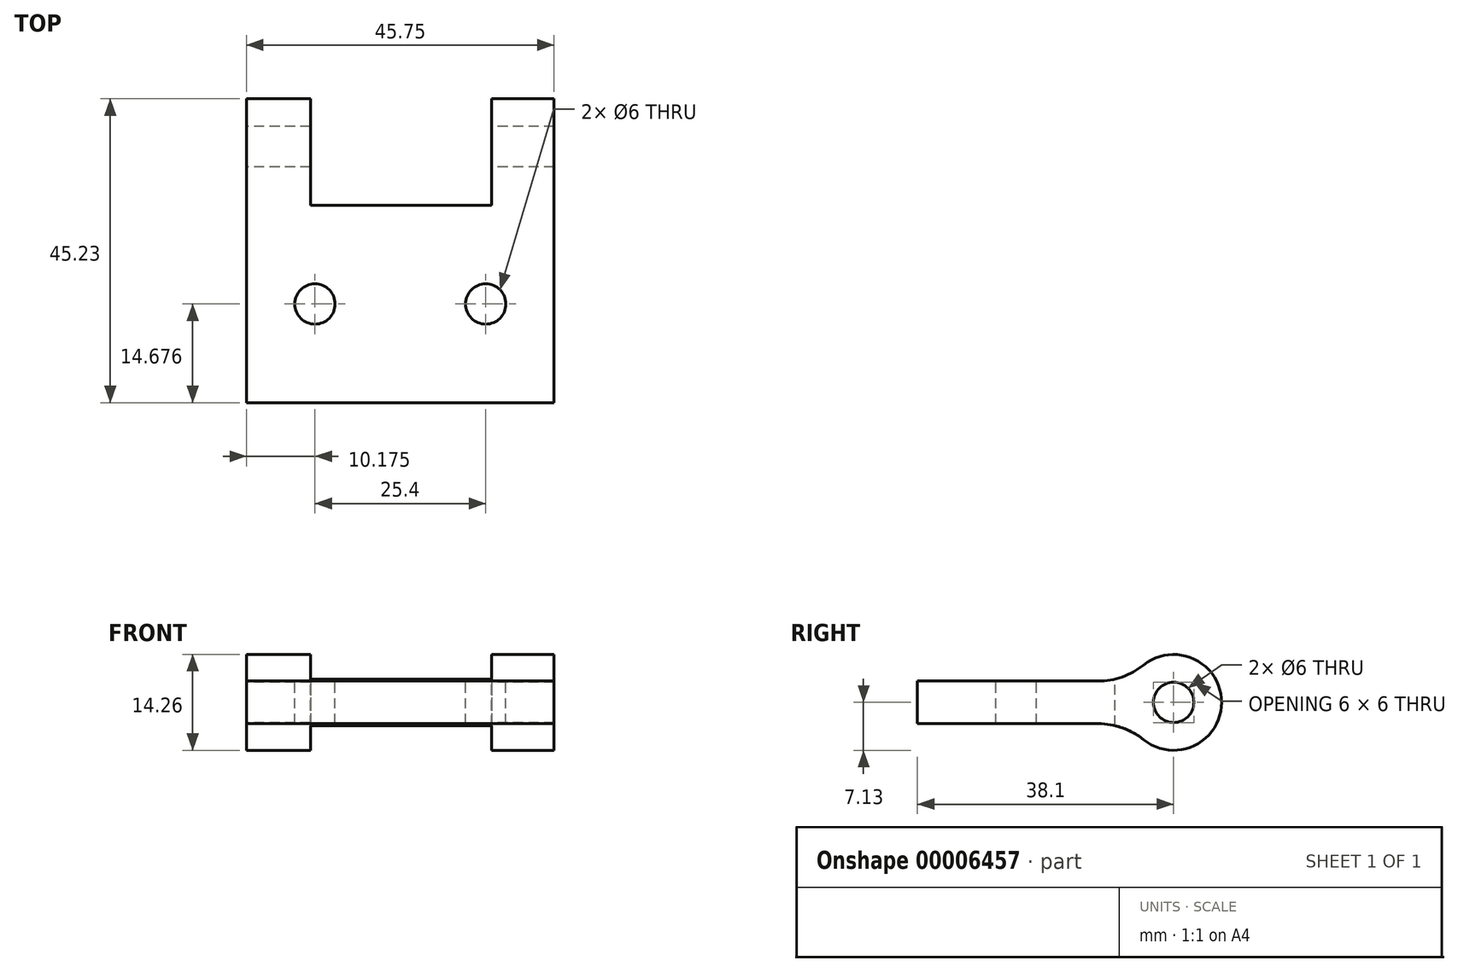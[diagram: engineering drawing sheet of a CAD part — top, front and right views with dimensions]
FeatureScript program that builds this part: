
annotation { "Feature Type Name" : "Feature", "Feature Type Description" : "" }
export const myFeature = defineFeature(function(context is Context, id is Id, definition is map)
    precondition{}
    {
        {
            var Q0;
            Q0=qCreatedBy(makeId("Right.planeOp"),FACE);
            var sketch = newSketch(context, id + "F0", { "sketchPlane" : qUnion([Q0])});
            skCircle(sketch, "E0", {"center": v(0, 0) * mm, "radius": 3 * mm});
            skArc(sketch, "E1", {"start": v(-6.38, -3.17) * mm, "mid": v(7.13, 0) * mm, "end": v(-6.38, 3.17) * mm});
            skLineSegment(sketch, "E2.bottom", {"start": v(-6.38, 3.17) * mm, "end": v(-38.1, 3.18) * mm});
            skLineSegment(sketch, "E2.top", {"start": v(-6.38, -3.17) * mm, "end": v(-38.1, -3.18) * mm});
            skLineSegment(sketch, "E2.right", {"start": v(-38.1, 3.18) * mm, "end": v(-38.1, -3.18) * mm});
            skSolve(sketch);
        }
        {
            var Q0;
            Q0 = qSketchRegion(id + "F0", true);
            extrude(context, id + "F1", {"entities" : qUnion([Q0]), "depth" : 45.75 * mm});
        }
        {
            var Q0;
            Q0=qCreatedBy(makeId("Top.planeOp"),FACE);
            var sketch = newSketch(context, id + "F2", { "sketchPlane" : qUnion([Q0])});
            skLineSegment(sketch, "E3.bottom", {"start": v(9.52, 7.13) * mm, "end": v(36.48, 7.13) * mm});
            skLineSegment(sketch, "E3.top", {"start": v(9.53, -8.75) * mm, "end": v(36.48, -8.75) * mm});
            skLineSegment(sketch, "E3.left", {"start": v(9.52, 7.13) * mm, "end": v(9.53, -8.75) * mm});
            skLineSegment(sketch, "E3.right", {"start": v(36.48, 7.13) * mm, "end": v(36.48, -8.75) * mm});
            skSolve(sketch);
        }
        {
            var Q0;
            Q0 = qSketchRegion(id + "F2", true);
            extrude(context, id + "F3", {"entities" : qUnion([Q0]), "operationType" : NewBodyOperationType.REMOVE, "endBound" : BoundingType.THROUGH_ALL, "oppositeDirection" : true, "depth" : 25.4 * mm, "hasSecondDirection" : true, "secondDirectionBound" : SecondDirectionBoundingType.THROUGH_ALL, "secondDirectionOppositeDirection" : false, "secondDirectionDepth" : 25.4 * mm});
        }
        {
            var Q0;
            Q0=makeQuery(id+"F1.opExtrude","SWEPT_FACE",FACE,{"disambiguationData":[OSD([sQuery(id+"F0.wireOp",EDGE,"E2.bottom")])]});
            var sketch = newSketch(context, id + "F4", { "sketchPlane" : qUnion([Q0])});
            skCircle(sketch, "E4", {"center": v(10.18, -23.42) * mm, "radius": 3 * mm});
            skCircle(sketch, "E5", {"center": v(35.58, -23.42) * mm, "radius": 3 * mm});
            skLineSegment(sketch, "E6", {"start": v(10.18, -23.42) * mm, "end": v(0, -23.42) * mm, "construction": true});
            skLineSegment(sketch, "E7", {"start": v(35.58, -23.42) * mm, "end": v(45.75, -23.42) * mm, "construction": true});
            skLineSegment(sketch, "E8", {"start": v(10.18, -23.42) * mm, "end": v(10.18, -8.75) * mm, "construction": true});
            skLineSegment(sketch, "E9", {"start": v(10.18, -23.42) * mm, "end": v(10.18, -38.1) * mm, "construction": true});
            skSolve(sketch);
        }
        {
            var Q0;
            Q0 = qSketchRegion(id + "F4", true);
            extrude(context, id + "F5", {"entities" : qUnion([Q0]), "operationType" : NewBodyOperationType.REMOVE, "endBound" : BoundingType.THROUGH_ALL, "oppositeDirection" : true, "depth" : 25.4 * mm});
        }
        {
            var Q0;
            {var subQ0=sQuery(id+"F0.wireOp",EDGE,"E1");var subQ1=sQuery(id+"F0.wireOp",EDGE,"E2.bottom");Q0=makeQuery(id+"F3.boolean.opBoolean","SPLIT",EDGE,{"disambiguationData":[TD([makeQuery(id+"F3.opExtrude","SWEPT_FACE",FACE,{"disambiguationData":[OSD([sQuery(id+"F2.wireOp",EDGE,"E3.right")])]})])],"derivedFrom":makeQuery(id+"F1.opExtrude","SWEPT_EDGE",EDGE,{"disambiguationData":[OSD([subQ0,subQ1])]})});}
            var Q1;
            {var subQ0=sQuery(id+"F0.wireOp",EDGE,"E1");var subQ1=sQuery(id+"F0.wireOp",EDGE,"E2.top");Q1=makeQuery(id+"F3.boolean.opBoolean","SPLIT",EDGE,{"disambiguationData":[TD([makeQuery(id+"F3.opExtrude","SWEPT_FACE",FACE,{"disambiguationData":[OSD([sQuery(id+"F2.wireOp",EDGE,"E3.left")])]})])],"derivedFrom":makeQuery(id+"F1.opExtrude","SWEPT_EDGE",EDGE,{"disambiguationData":[OSD([subQ0,subQ1])]})});}
            fillet(context, id + "F6", {"entities" : qUnion([Q0, Q1]), "radius" : 10.8 * mm, "tangentPropagation" : true, "allowEdgeOverflow" : false});
        }
    });
